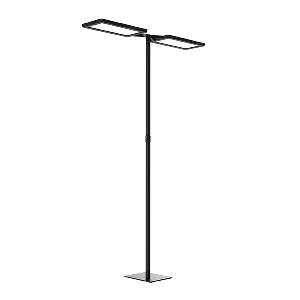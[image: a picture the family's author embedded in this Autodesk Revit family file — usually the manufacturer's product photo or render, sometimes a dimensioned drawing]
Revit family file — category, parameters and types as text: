
# Revit family: yara_doublet_-_yts_2_6000_840_r_sw_cee_00_c_114268000-00808317_e33a
name_source: partatom
category: Lighting Fixtures
units: mm (PartAtom-declared; Revit-internal decimal feet)

## family parameters
Cut with Voids When Loaded = No
Host = Face
Light Source = No
Part Type = Normal
Room Calculation Point = No
Round Connector Dimension = Use Diameter
Shared = No

## types (1)
- YARA.doubleT - YTS 2/6000/840/R/SW/CEE/00/C (1 x LED, 6000 lm, 4000K)
    Apparent Load = 84 VA
    Approval mark = CE
    CIE Flux Codes = 58 87 97 13 100
    Color Rendering = 80-89
    Color Temperature = 4000K
    Control Gear = Electronic ballast
    Default Elevation = 1800 mm
    Description = YTS 2/6000/840/R/SW/CEE/00/R|Free-standing luminaire|light source: LED|work equipment: Electronic ballast DALI|connected load: 220-240 V, 50/60 Hz|Power consumption: approx. 83 W|power factor: approx. 0,966|luminous flux: 12000 lm|luminous efficacy: 144 lm/W|light distribution: Direct/indirect|direct ratio: approx. 13 %|colour temperature: Cold white, ca. 4000 K|color rendering index (CRI): >= 80|chromaticity tolerance:  3 SDCM|technology: Presence and daylight sensor control (PIR)|operation: Wireless switch|luminaire body|material: Aluminium/plastic|surface: Powder coatet|colour: Black|lamp cover: Acrylic (PMMA), Satine, Structured|tubular section|material: Steel tube|surface: Powder-coated|Form: Tubular section upright|colour of tubular section: Black|luminaire base|Form: Rectangular flat|weight (net): approx. 24.0 kg|mains lead: 3.00 m Mains plug CEE 7/VII|Fastening: Floor standing base|glare control: Conical prismatic screen|luminance(L65): <= 1100 cd/m|unified glare rating(4H 8H): <=  16|special features: App control, Asymmetric radiation, Direct and indirect lighting component with edge light and light guidetechnology for a homogeneous light exit, Flicker-free, Magnetic control panel, freely positionable, PIR movement and daylight sensor|Approval mark: VDE - ENEC|
    Frequency = 50 Hz, 60 Hz
    Height = 24 mm  [stored 0.0787402 ft]
    Lamp = 1 x LED
    Lamp Light Flux = 6000 lm
    Lamp count = 1
    Length = 690 mm
    Luminous efficacy = 143 lm/W
    Manufacturer = Waldmann
    ModVariant = No
    Model = 114268000-00808317
    Mounting Place = Floor
    Mounting Type = Freestanding
    Number of Poles = 1
    OnlyDefault = Yes
    Power Factor = 1
    Product Name = YARA.doubleT - YTS 2/6000/840/R/SW/CEE/00/C
    Product group = Free standing luminaire
    ProductGroupID = 13
    Protection Class = Protection class I
    Protection Degree = IP 20
    RLX_Detail_Level = 1
    RlxData = <blob elided: 64405 chars, md5=566d057d>
    Socket = socket
    Standby Power = 0 W
    System Light Flux = 12000 lm
    System Power = 84 W
    Type Comments = Product without accessories
    Type Image = yts-r-sw-r.jpg
    URL = http://relux.com
    VarID = ---
    Voltage = 230 V
    Voltage Range = 220-240 V
    Weight = 0.00 kg
    Width = 358 mm

note: [stored X ft] marks values corroborated as IEEE doubles in the binary element streams (Revit-internal decimal feet)

## geometry (parser evidence)
native form markers: Blend x4, Sweep x20
no freeform markers — native parametric forms only
